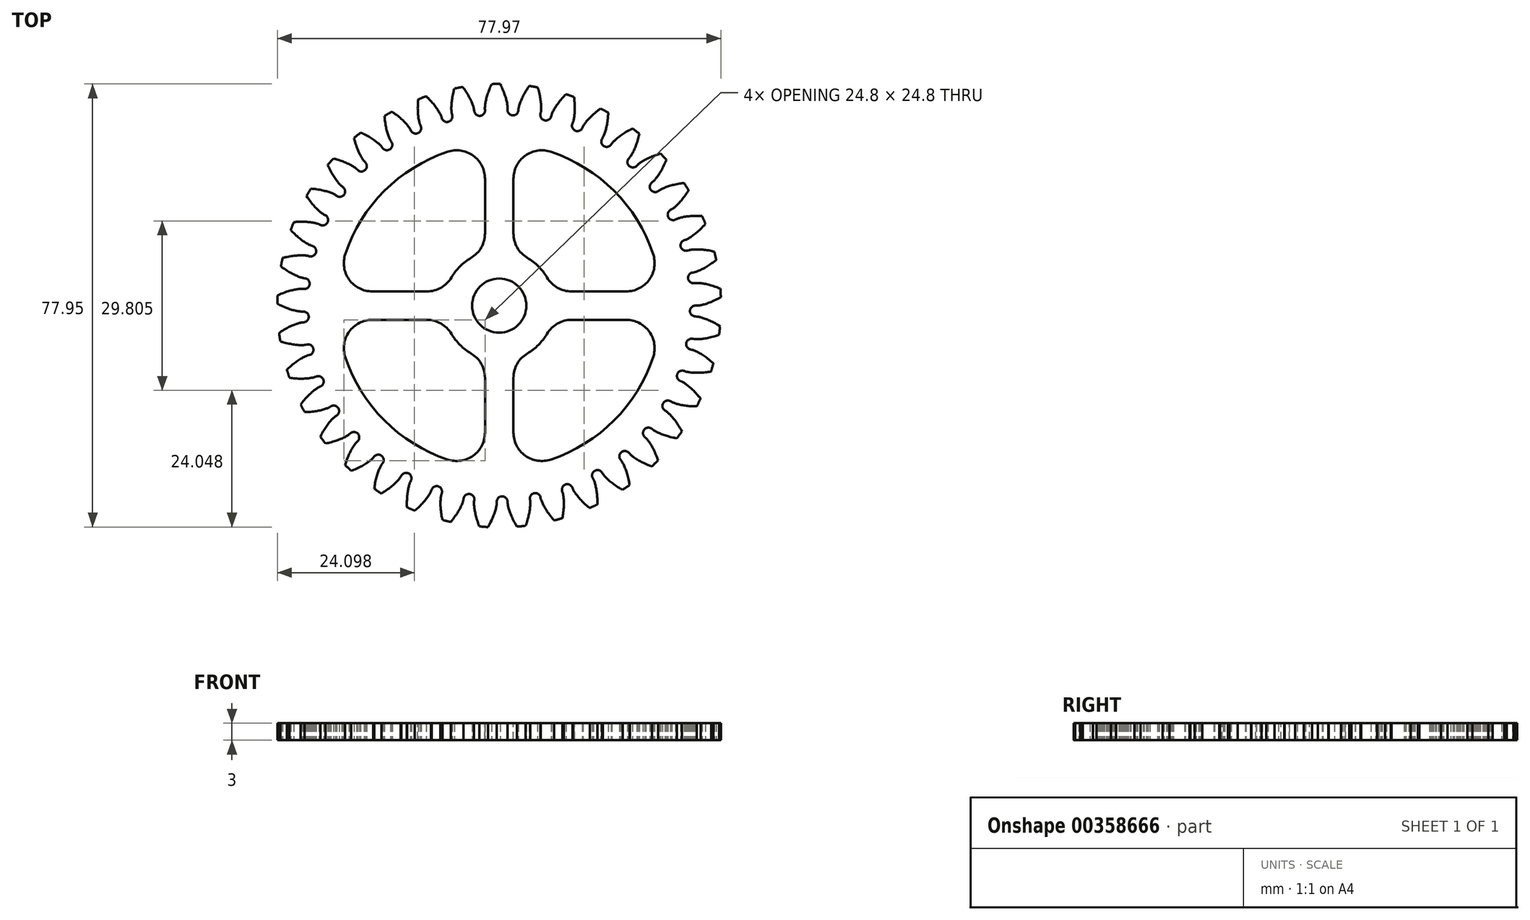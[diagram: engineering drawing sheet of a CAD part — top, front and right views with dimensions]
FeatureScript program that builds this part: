
annotation { "Feature Type Name" : "Feature", "Feature Type Description" : "" }
export const myFeature = defineFeature(function(context is Context, id is Id, definition is map)
    precondition{}
    {
        {
            assignVariable(context, id + "F0", {"name" : "T", "anyValue" : 37});
        }
        {
            assignVariable(context, id + "F1", {"name" : "SP", "anyValue" : 4});
        }
        {
            var Q0;
            Q0=qCreatedBy(makeId("Top.planeOp"),FACE);
            var sketch = newSketch(context, id + "F2", { "sketchPlane" : qUnion([Q0])});
            skCircle(sketch, "E0", {"center": v(0, 0) * mm, "radius": 39 * mm});
            skCircle(sketch, "E1", {"center": v(0, 0) * mm, "radius": 37 * mm, "construction": true});
            skCircle(sketch, "E2", {"center": v(0, 0) * mm, "radius": 34.77 * mm, "construction": true});
            skCircle(sketch, "E3", {"center": v(0, 0) * mm, "radius": 34.5 * mm});
            skLineSegment(sketch, "E4", {"start": v(0, 0) * mm, "end": v(34.77, 0) * mm});
            skFitSpline(sketch, "E5", {"points": [v(34.77, 0) * mm, v(34.82, 0) * mm, v(34.97, 0.01) * mm, v(35.21, 0.05) * mm, v(35.55, 0.11) * mm, v(35.98, 0.22) * mm, v(36.5, 0.38) * mm, v(37.1, 0.6) * mm, v(37.8, 0.88) * mm, v(38.55, 1.25) * mm, v(39.37, 1.71) * mm], "startDerivative": vector(4.43, 0.16) * mm, "endDerivative": vector(16.9, 9.4) * mm});
            skLineSegment(sketch, "E6", {"start": v(0, 0) * mm, "end": v(38.99, -1.07) * mm, "construction": true});
            skLineSegment(sketch, "E7", {"start": v(0, 0) * mm, "end": v(37, 0.55) * mm, "construction": true});
            skFitSpline(sketch, "E8.MirrorCS", {"points": [v(34.72, -1.91) * mm, v(34.77, -1.92) * mm, v(34.91, -1.94) * mm, v(35.16, -1.99) * mm, v(35.5, -2.07) * mm, v(35.92, -2.2) * mm, v(36.43, -2.39) * mm, v(37.02, -2.64) * mm, v(37.69, -2.96) * mm, v(38.42, -3.37) * mm, v(39.22, -3.88) * mm], "startDerivative": vector(4.42, -0.4) * mm, "endDerivative": vector(16.36, -10.31) * mm});
            skLineSegment(sketch, "E9", {"start": v(0, 0) * mm, "end": v(34.72, -1.91) * mm});
            skSolve(sketch);
        }
        {
            var Q0;
            Q0=qCreatedBy(makeId("Top.planeOp"),FACE);
            var sketch = newSketch(context, id + "F3", { "sketchPlane" : qUnion([Q0])});
            skCircle(sketch, "E10", {"center": v(0, 0) * mm, "radius": 39 * mm});
            skSolve(sketch);
        }
        {
            var Q0;
            {var subQ0=sQuery(id+"F2.wireOp",EDGE,"E5");var subQ7=sQuery(id+"F2.wireOp",EDGE,"E0");var subQ8=makeQuery(id+"F2.imprint","INTERSECT",VERTEX,{"derivedFrom":[subQ7,subQ0]});Q0=makeQuery(id+"F2.imprint","IMPRINT",FACE,{"disambiguationData":[TD([[makeQuery(id+"F2.imprint","IMPRINT",EDGE,{"disambiguationData":[TD([[subQ8,1.0]])],"derivedFrom":subQ7}),1.0]])]});}
            extrude(context, id + "F4", {"entities" : qUnion([Q0]), "depth" : 6 * mm});
        }
        {
            var Q0;
            Q0=makeQuery(id+"F4.opExtrude","CAP_FACE",FACE,{"disambiguationData":[OSD([sQuery(id+"F2.wireOp",EDGE,"E0"),sQuery(id+"F2.wireOp",EDGE,"E3"),sQuery(id+"F2.wireOp",EDGE,"E4"),sQuery(id+"F2.wireOp",EDGE,"E5"),sQuery(id+"F2.wireOp",EDGE,"E8.MirrorCS"),sQuery(id+"F2.wireOp",EDGE,"E9")])],"isStart":true});
            var sketch = newSketch(context, id + "F5", { "sketchPlane" : qUnion([Q0])});
            skCircle(sketch, "E11", {"center": v(34.49, 0.95) * mm, "radius": 0.95 * mm});
            skSolve(sketch);
        }
        {
            var Q0;
            {var subQ1=makeQuery(id+"F4.opExtrude","CAP_EDGE",EDGE,{"disambiguationData":[OSD([sQuery(id+"F2.wireOp",EDGE,"E3")])],"isStart":true});Q0=makeQuery(id+"F5.imprint","IMPRINT",FACE,{"disambiguationData":[TD([[makeQuery(id+"F5.imprint","IMPRINT",EDGE,{"derivedFrom":subQ1}),-1.0]])]});}
            extrude(context, id + "F6", {"entities" : qUnion([Q0]), "operationType" : NewBodyOperationType.ADD, "oppositeDirection" : true, "depth" : 6 * mm});
        }
        {
            var Q0;
            Q0=makeQuery(id+"F3.imprint","IMPRINT",FACE,{"disambiguationData":[TD([[makeQuery(id+"F3.imprint","IMPRINT",EDGE,{"derivedFrom":sQuery(id+"F3.wireOp",EDGE,"E10")}),1.0]])]});
            extrude(context, id + "F7", {"entities" : qUnion([Q0]), "depth" : 3 * mm, "offsetDistance" : 25 * mm});
        }
        {
            var Q0;
            Q0=makeQuery(id+"F4.opExtrude","SWEPT_BODY",BODY,{"disambiguationData":[OSD([sQuery(id+"F2.wireOp",EDGE,"E0"),sQuery(id+"F2.wireOp",EDGE,"E3"),sQuery(id+"F2.wireOp",EDGE,"E4"),sQuery(id+"F2.wireOp",EDGE,"E5"),sQuery(id+"F2.wireOp",EDGE,"E8.MirrorCS"),sQuery(id+"F2.wireOp",EDGE,"E9")])]});
            var Q1;
            Q1=makeQuery(id+"F7.opExtrude","CAP_EDGE",EDGE,{"disambiguationData":[OSD([sQuery(id+"F3.wireOp",EDGE,"E10")])],"isStart":false});
            circularPattern(context, id + "F8", {"entities" : qUnion([Q0]), "axis" : qUnion([Q1]), "angle" : 360 * degree, "instanceCount" : getVariable(context, 'T'), "equalSpace" : true});
        }
        {
            var Q0;
            Q0=makeQuery(id+"F8.opPattern","COPY",BODY,{"derivedFrom":makeQuery(id+"F4.opExtrude","SWEPT_BODY",BODY,{"disambiguationData":[OSD([sQuery(id+"F2.wireOp",EDGE,"E0"),sQuery(id+"F2.wireOp",EDGE,"E3"),sQuery(id+"F2.wireOp",EDGE,"E4"),sQuery(id+"F2.wireOp",EDGE,"E5"),sQuery(id+"F2.wireOp",EDGE,"E8.MirrorCS"),sQuery(id+"F2.wireOp",EDGE,"E9")])]}),"instanceName":"5"});
            var Q1;
            Q1=makeQuery(id+"F8.opPattern","COPY",BODY,{"derivedFrom":makeQuery(id+"F4.opExtrude","SWEPT_BODY",BODY,{"disambiguationData":[OSD([sQuery(id+"F2.wireOp",EDGE,"E0"),sQuery(id+"F2.wireOp",EDGE,"E3"),sQuery(id+"F2.wireOp",EDGE,"E4"),sQuery(id+"F2.wireOp",EDGE,"E5"),sQuery(id+"F2.wireOp",EDGE,"E8.MirrorCS"),sQuery(id+"F2.wireOp",EDGE,"E9")])]}),"instanceName":"6"});
            var Q2;
            Q2=makeQuery(id+"F8.opPattern","COPY",BODY,{"derivedFrom":makeQuery(id+"F4.opExtrude","SWEPT_BODY",BODY,{"disambiguationData":[OSD([sQuery(id+"F2.wireOp",EDGE,"E0"),sQuery(id+"F2.wireOp",EDGE,"E3"),sQuery(id+"F2.wireOp",EDGE,"E4"),sQuery(id+"F2.wireOp",EDGE,"E5"),sQuery(id+"F2.wireOp",EDGE,"E8.MirrorCS"),sQuery(id+"F2.wireOp",EDGE,"E9")])]}),"instanceName":"7"});
            var Q3;
            Q3=makeQuery(id+"F8.opPattern","COPY",BODY,{"derivedFrom":makeQuery(id+"F4.opExtrude","SWEPT_BODY",BODY,{"disambiguationData":[OSD([sQuery(id+"F2.wireOp",EDGE,"E0"),sQuery(id+"F2.wireOp",EDGE,"E3"),sQuery(id+"F2.wireOp",EDGE,"E4"),sQuery(id+"F2.wireOp",EDGE,"E5"),sQuery(id+"F2.wireOp",EDGE,"E8.MirrorCS"),sQuery(id+"F2.wireOp",EDGE,"E9")])]}),"instanceName":"8"});
            var Q4;
            Q4=makeQuery(id+"F8.opPattern","COPY",BODY,{"derivedFrom":makeQuery(id+"F4.opExtrude","SWEPT_BODY",BODY,{"disambiguationData":[OSD([sQuery(id+"F2.wireOp",EDGE,"E0"),sQuery(id+"F2.wireOp",EDGE,"E3"),sQuery(id+"F2.wireOp",EDGE,"E4"),sQuery(id+"F2.wireOp",EDGE,"E5"),sQuery(id+"F2.wireOp",EDGE,"E8.MirrorCS"),sQuery(id+"F2.wireOp",EDGE,"E9")])]}),"instanceName":"9"});
            var Q5;
            Q5=makeQuery(id+"F8.opPattern","COPY",BODY,{"derivedFrom":makeQuery(id+"F4.opExtrude","SWEPT_BODY",BODY,{"disambiguationData":[OSD([sQuery(id+"F2.wireOp",EDGE,"E0"),sQuery(id+"F2.wireOp",EDGE,"E3"),sQuery(id+"F2.wireOp",EDGE,"E4"),sQuery(id+"F2.wireOp",EDGE,"E5"),sQuery(id+"F2.wireOp",EDGE,"E8.MirrorCS"),sQuery(id+"F2.wireOp",EDGE,"E9")])]}),"instanceName":"10"});
            var Q6;
            Q6=makeQuery(id+"F8.opPattern","COPY",BODY,{"derivedFrom":makeQuery(id+"F4.opExtrude","SWEPT_BODY",BODY,{"disambiguationData":[OSD([sQuery(id+"F2.wireOp",EDGE,"E0"),sQuery(id+"F2.wireOp",EDGE,"E3"),sQuery(id+"F2.wireOp",EDGE,"E4"),sQuery(id+"F2.wireOp",EDGE,"E5"),sQuery(id+"F2.wireOp",EDGE,"E8.MirrorCS"),sQuery(id+"F2.wireOp",EDGE,"E9")])]}),"instanceName":"11"});
            var Q7;
            Q7=makeQuery(id+"F8.opPattern","COPY",BODY,{"derivedFrom":makeQuery(id+"F4.opExtrude","SWEPT_BODY",BODY,{"disambiguationData":[OSD([sQuery(id+"F2.wireOp",EDGE,"E0"),sQuery(id+"F2.wireOp",EDGE,"E3"),sQuery(id+"F2.wireOp",EDGE,"E4"),sQuery(id+"F2.wireOp",EDGE,"E5"),sQuery(id+"F2.wireOp",EDGE,"E8.MirrorCS"),sQuery(id+"F2.wireOp",EDGE,"E9")])]}),"instanceName":"12"});
            var Q8;
            Q8=makeQuery(id+"F8.opPattern","COPY",BODY,{"derivedFrom":makeQuery(id+"F4.opExtrude","SWEPT_BODY",BODY,{"disambiguationData":[OSD([sQuery(id+"F2.wireOp",EDGE,"E0"),sQuery(id+"F2.wireOp",EDGE,"E3"),sQuery(id+"F2.wireOp",EDGE,"E4"),sQuery(id+"F2.wireOp",EDGE,"E5"),sQuery(id+"F2.wireOp",EDGE,"E8.MirrorCS"),sQuery(id+"F2.wireOp",EDGE,"E9")])]}),"instanceName":"13"});
            var Q9;
            Q9=makeQuery(id+"F8.opPattern","COPY",BODY,{"derivedFrom":makeQuery(id+"F4.opExtrude","SWEPT_BODY",BODY,{"disambiguationData":[OSD([sQuery(id+"F2.wireOp",EDGE,"E0"),sQuery(id+"F2.wireOp",EDGE,"E3"),sQuery(id+"F2.wireOp",EDGE,"E4"),sQuery(id+"F2.wireOp",EDGE,"E5"),sQuery(id+"F2.wireOp",EDGE,"E8.MirrorCS"),sQuery(id+"F2.wireOp",EDGE,"E9")])]}),"instanceName":"14"});
            var Q10;
            Q10=makeQuery(id+"F8.opPattern","COPY",BODY,{"derivedFrom":makeQuery(id+"F4.opExtrude","SWEPT_BODY",BODY,{"disambiguationData":[OSD([sQuery(id+"F2.wireOp",EDGE,"E0"),sQuery(id+"F2.wireOp",EDGE,"E3"),sQuery(id+"F2.wireOp",EDGE,"E4"),sQuery(id+"F2.wireOp",EDGE,"E5"),sQuery(id+"F2.wireOp",EDGE,"E8.MirrorCS"),sQuery(id+"F2.wireOp",EDGE,"E9")])]}),"instanceName":"15"});
            var Q11;
            Q11=makeQuery(id+"F8.opPattern","COPY",BODY,{"derivedFrom":makeQuery(id+"F4.opExtrude","SWEPT_BODY",BODY,{"disambiguationData":[OSD([sQuery(id+"F2.wireOp",EDGE,"E0"),sQuery(id+"F2.wireOp",EDGE,"E3"),sQuery(id+"F2.wireOp",EDGE,"E4"),sQuery(id+"F2.wireOp",EDGE,"E5"),sQuery(id+"F2.wireOp",EDGE,"E8.MirrorCS"),sQuery(id+"F2.wireOp",EDGE,"E9")])]}),"instanceName":"16"});
            var Q12;
            Q12=makeQuery(id+"F8.opPattern","COPY",BODY,{"derivedFrom":makeQuery(id+"F4.opExtrude","SWEPT_BODY",BODY,{"disambiguationData":[OSD([sQuery(id+"F2.wireOp",EDGE,"E0"),sQuery(id+"F2.wireOp",EDGE,"E3"),sQuery(id+"F2.wireOp",EDGE,"E4"),sQuery(id+"F2.wireOp",EDGE,"E5"),sQuery(id+"F2.wireOp",EDGE,"E8.MirrorCS"),sQuery(id+"F2.wireOp",EDGE,"E9")])]}),"instanceName":"17"});
            var Q13;
            Q13=makeQuery(id+"F8.opPattern","COPY",BODY,{"derivedFrom":makeQuery(id+"F4.opExtrude","SWEPT_BODY",BODY,{"disambiguationData":[OSD([sQuery(id+"F2.wireOp",EDGE,"E0"),sQuery(id+"F2.wireOp",EDGE,"E3"),sQuery(id+"F2.wireOp",EDGE,"E4"),sQuery(id+"F2.wireOp",EDGE,"E5"),sQuery(id+"F2.wireOp",EDGE,"E8.MirrorCS"),sQuery(id+"F2.wireOp",EDGE,"E9")])]}),"instanceName":"18"});
            var Q14;
            Q14=makeQuery(id+"F8.opPattern","COPY",BODY,{"derivedFrom":makeQuery(id+"F4.opExtrude","SWEPT_BODY",BODY,{"disambiguationData":[OSD([sQuery(id+"F2.wireOp",EDGE,"E0"),sQuery(id+"F2.wireOp",EDGE,"E3"),sQuery(id+"F2.wireOp",EDGE,"E4"),sQuery(id+"F2.wireOp",EDGE,"E5"),sQuery(id+"F2.wireOp",EDGE,"E8.MirrorCS"),sQuery(id+"F2.wireOp",EDGE,"E9")])]}),"instanceName":"19"});
            var Q15;
            Q15=makeQuery(id+"F8.opPattern","COPY",BODY,{"derivedFrom":makeQuery(id+"F4.opExtrude","SWEPT_BODY",BODY,{"disambiguationData":[OSD([sQuery(id+"F2.wireOp",EDGE,"E0"),sQuery(id+"F2.wireOp",EDGE,"E3"),sQuery(id+"F2.wireOp",EDGE,"E4"),sQuery(id+"F2.wireOp",EDGE,"E5"),sQuery(id+"F2.wireOp",EDGE,"E8.MirrorCS"),sQuery(id+"F2.wireOp",EDGE,"E9")])]}),"instanceName":"20"});
            var Q16;
            Q16=makeQuery(id+"F8.opPattern","COPY",BODY,{"derivedFrom":makeQuery(id+"F4.opExtrude","SWEPT_BODY",BODY,{"disambiguationData":[OSD([sQuery(id+"F2.wireOp",EDGE,"E0"),sQuery(id+"F2.wireOp",EDGE,"E3"),sQuery(id+"F2.wireOp",EDGE,"E4"),sQuery(id+"F2.wireOp",EDGE,"E5"),sQuery(id+"F2.wireOp",EDGE,"E8.MirrorCS"),sQuery(id+"F2.wireOp",EDGE,"E9")])]}),"instanceName":"21"});
            var Q17;
            Q17=makeQuery(id+"F8.opPattern","COPY",BODY,{"derivedFrom":makeQuery(id+"F4.opExtrude","SWEPT_BODY",BODY,{"disambiguationData":[OSD([sQuery(id+"F2.wireOp",EDGE,"E0"),sQuery(id+"F2.wireOp",EDGE,"E3"),sQuery(id+"F2.wireOp",EDGE,"E4"),sQuery(id+"F2.wireOp",EDGE,"E5"),sQuery(id+"F2.wireOp",EDGE,"E8.MirrorCS"),sQuery(id+"F2.wireOp",EDGE,"E9")])]}),"instanceName":"22"});
            var Q18;
            Q18=makeQuery(id+"F8.opPattern","COPY",BODY,{"derivedFrom":makeQuery(id+"F4.opExtrude","SWEPT_BODY",BODY,{"disambiguationData":[OSD([sQuery(id+"F2.wireOp",EDGE,"E0"),sQuery(id+"F2.wireOp",EDGE,"E3"),sQuery(id+"F2.wireOp",EDGE,"E4"),sQuery(id+"F2.wireOp",EDGE,"E5"),sQuery(id+"F2.wireOp",EDGE,"E8.MirrorCS"),sQuery(id+"F2.wireOp",EDGE,"E9")])]}),"instanceName":"23"});
            var Q19;
            Q19=makeQuery(id+"F8.opPattern","COPY",BODY,{"derivedFrom":makeQuery(id+"F4.opExtrude","SWEPT_BODY",BODY,{"disambiguationData":[OSD([sQuery(id+"F2.wireOp",EDGE,"E0"),sQuery(id+"F2.wireOp",EDGE,"E3"),sQuery(id+"F2.wireOp",EDGE,"E4"),sQuery(id+"F2.wireOp",EDGE,"E5"),sQuery(id+"F2.wireOp",EDGE,"E8.MirrorCS"),sQuery(id+"F2.wireOp",EDGE,"E9")])]}),"instanceName":"24"});
            var Q20;
            Q20=makeQuery(id+"F8.opPattern","COPY",BODY,{"derivedFrom":makeQuery(id+"F4.opExtrude","SWEPT_BODY",BODY,{"disambiguationData":[OSD([sQuery(id+"F2.wireOp",EDGE,"E0"),sQuery(id+"F2.wireOp",EDGE,"E3"),sQuery(id+"F2.wireOp",EDGE,"E4"),sQuery(id+"F2.wireOp",EDGE,"E5"),sQuery(id+"F2.wireOp",EDGE,"E8.MirrorCS"),sQuery(id+"F2.wireOp",EDGE,"E9")])]}),"instanceName":"25"});
            var Q21;
            Q21=makeQuery(id+"F8.opPattern","COPY",BODY,{"derivedFrom":makeQuery(id+"F4.opExtrude","SWEPT_BODY",BODY,{"disambiguationData":[OSD([sQuery(id+"F2.wireOp",EDGE,"E0"),sQuery(id+"F2.wireOp",EDGE,"E3"),sQuery(id+"F2.wireOp",EDGE,"E4"),sQuery(id+"F2.wireOp",EDGE,"E5"),sQuery(id+"F2.wireOp",EDGE,"E8.MirrorCS"),sQuery(id+"F2.wireOp",EDGE,"E9")])]}),"instanceName":"26"});
            var Q22;
            Q22=makeQuery(id+"F8.opPattern","COPY",BODY,{"derivedFrom":makeQuery(id+"F4.opExtrude","SWEPT_BODY",BODY,{"disambiguationData":[OSD([sQuery(id+"F2.wireOp",EDGE,"E0"),sQuery(id+"F2.wireOp",EDGE,"E3"),sQuery(id+"F2.wireOp",EDGE,"E4"),sQuery(id+"F2.wireOp",EDGE,"E5"),sQuery(id+"F2.wireOp",EDGE,"E8.MirrorCS"),sQuery(id+"F2.wireOp",EDGE,"E9")])]}),"instanceName":"27"});
            var Q23;
            Q23=makeQuery(id+"F8.opPattern","COPY",BODY,{"derivedFrom":makeQuery(id+"F4.opExtrude","SWEPT_BODY",BODY,{"disambiguationData":[OSD([sQuery(id+"F2.wireOp",EDGE,"E0"),sQuery(id+"F2.wireOp",EDGE,"E3"),sQuery(id+"F2.wireOp",EDGE,"E4"),sQuery(id+"F2.wireOp",EDGE,"E5"),sQuery(id+"F2.wireOp",EDGE,"E8.MirrorCS"),sQuery(id+"F2.wireOp",EDGE,"E9")])]}),"instanceName":"28"});
            var Q24;
            Q24=makeQuery(id+"F8.opPattern","COPY",BODY,{"derivedFrom":makeQuery(id+"F4.opExtrude","SWEPT_BODY",BODY,{"disambiguationData":[OSD([sQuery(id+"F2.wireOp",EDGE,"E0"),sQuery(id+"F2.wireOp",EDGE,"E3"),sQuery(id+"F2.wireOp",EDGE,"E4"),sQuery(id+"F2.wireOp",EDGE,"E5"),sQuery(id+"F2.wireOp",EDGE,"E8.MirrorCS"),sQuery(id+"F2.wireOp",EDGE,"E9")])]}),"instanceName":"29"});
            var Q25;
            Q25=makeQuery(id+"F4.opExtrude","SWEPT_BODY",BODY,{"disambiguationData":[OSD([sQuery(id+"F2.wireOp",EDGE,"E0"),sQuery(id+"F2.wireOp",EDGE,"E3"),sQuery(id+"F2.wireOp",EDGE,"E4"),sQuery(id+"F2.wireOp",EDGE,"E5"),sQuery(id+"F2.wireOp",EDGE,"E8.MirrorCS"),sQuery(id+"F2.wireOp",EDGE,"E9")])]});
            var Q26;
            Q26=makeQuery(id+"F8.opPattern","COPY",BODY,{"derivedFrom":makeQuery(id+"F4.opExtrude","SWEPT_BODY",BODY,{"disambiguationData":[OSD([sQuery(id+"F2.wireOp",EDGE,"E0"),sQuery(id+"F2.wireOp",EDGE,"E3"),sQuery(id+"F2.wireOp",EDGE,"E4"),sQuery(id+"F2.wireOp",EDGE,"E5"),sQuery(id+"F2.wireOp",EDGE,"E8.MirrorCS"),sQuery(id+"F2.wireOp",EDGE,"E9")])]}),"instanceName":"1"});
            var Q27;
            Q27=makeQuery(id+"F8.opPattern","COPY",BODY,{"derivedFrom":makeQuery(id+"F4.opExtrude","SWEPT_BODY",BODY,{"disambiguationData":[OSD([sQuery(id+"F2.wireOp",EDGE,"E0"),sQuery(id+"F2.wireOp",EDGE,"E3"),sQuery(id+"F2.wireOp",EDGE,"E4"),sQuery(id+"F2.wireOp",EDGE,"E5"),sQuery(id+"F2.wireOp",EDGE,"E8.MirrorCS"),sQuery(id+"F2.wireOp",EDGE,"E9")])]}),"instanceName":"2"});
            var Q28;
            Q28=makeQuery(id+"F8.opPattern","COPY",BODY,{"derivedFrom":makeQuery(id+"F4.opExtrude","SWEPT_BODY",BODY,{"disambiguationData":[OSD([sQuery(id+"F2.wireOp",EDGE,"E0"),sQuery(id+"F2.wireOp",EDGE,"E3"),sQuery(id+"F2.wireOp",EDGE,"E4"),sQuery(id+"F2.wireOp",EDGE,"E5"),sQuery(id+"F2.wireOp",EDGE,"E8.MirrorCS"),sQuery(id+"F2.wireOp",EDGE,"E9")])]}),"instanceName":"3"});
            var Q29;
            Q29=makeQuery(id+"F8.opPattern","COPY",BODY,{"derivedFrom":makeQuery(id+"F4.opExtrude","SWEPT_BODY",BODY,{"disambiguationData":[OSD([sQuery(id+"F2.wireOp",EDGE,"E0"),sQuery(id+"F2.wireOp",EDGE,"E3"),sQuery(id+"F2.wireOp",EDGE,"E4"),sQuery(id+"F2.wireOp",EDGE,"E5"),sQuery(id+"F2.wireOp",EDGE,"E8.MirrorCS"),sQuery(id+"F2.wireOp",EDGE,"E9")])]}),"instanceName":"4"});
            var Q30;
            Q30=makeQuery(id+"F8.opPattern","COPY",BODY,{"derivedFrom":makeQuery(id+"F4.opExtrude","SWEPT_BODY",BODY,{"disambiguationData":[OSD([sQuery(id+"F2.wireOp",EDGE,"E0"),sQuery(id+"F2.wireOp",EDGE,"E3"),sQuery(id+"F2.wireOp",EDGE,"E5"),sQuery(id+"F2.wireOp",EDGE,"E8.MirrorCS")])]}),"instanceName":"30"});
            var Q31;
            Q31=makeQuery(id+"F8.opPattern","COPY",BODY,{"derivedFrom":makeQuery(id+"F4.opExtrude","SWEPT_BODY",BODY,{"disambiguationData":[OSD([sQuery(id+"F2.wireOp",EDGE,"E0"),sQuery(id+"F2.wireOp",EDGE,"E3"),sQuery(id+"F2.wireOp",EDGE,"E5"),sQuery(id+"F2.wireOp",EDGE,"E8.MirrorCS")])]}),"instanceName":"31"});
            var Q32;
            Q32=makeQuery(id+"F8.opPattern","COPY",BODY,{"derivedFrom":makeQuery(id+"F4.opExtrude","SWEPT_BODY",BODY,{"disambiguationData":[OSD([sQuery(id+"F2.wireOp",EDGE,"E0"),sQuery(id+"F2.wireOp",EDGE,"E3"),sQuery(id+"F2.wireOp",EDGE,"E5"),sQuery(id+"F2.wireOp",EDGE,"E8.MirrorCS")])]}),"instanceName":"32"});
            var Q33;
            Q33=makeQuery(id+"F8.opPattern","COPY",BODY,{"derivedFrom":makeQuery(id+"F4.opExtrude","SWEPT_BODY",BODY,{"disambiguationData":[OSD([sQuery(id+"F2.wireOp",EDGE,"E0"),sQuery(id+"F2.wireOp",EDGE,"E3"),sQuery(id+"F2.wireOp",EDGE,"E5"),sQuery(id+"F2.wireOp",EDGE,"E8.MirrorCS")])]}),"instanceName":"33"});
            var Q34;
            Q34=makeQuery(id+"F8.opPattern","COPY",BODY,{"derivedFrom":makeQuery(id+"F4.opExtrude","SWEPT_BODY",BODY,{"disambiguationData":[OSD([sQuery(id+"F2.wireOp",EDGE,"E0"),sQuery(id+"F2.wireOp",EDGE,"E3"),sQuery(id+"F2.wireOp",EDGE,"E5"),sQuery(id+"F2.wireOp",EDGE,"E8.MirrorCS")])]}),"instanceName":"34"});
            var Q35;
            Q35=makeQuery(id+"F8.opPattern","COPY",BODY,{"derivedFrom":makeQuery(id+"F4.opExtrude","SWEPT_BODY",BODY,{"disambiguationData":[OSD([sQuery(id+"F2.wireOp",EDGE,"E0"),sQuery(id+"F2.wireOp",EDGE,"E3"),sQuery(id+"F2.wireOp",EDGE,"E5"),sQuery(id+"F2.wireOp",EDGE,"E8.MirrorCS")])]}),"instanceName":"35"});
            var Q36;
            Q36=makeQuery(id+"F8.opPattern","COPY",BODY,{"derivedFrom":makeQuery(id+"F4.opExtrude","SWEPT_BODY",BODY,{"disambiguationData":[OSD([sQuery(id+"F2.wireOp",EDGE,"E0"),sQuery(id+"F2.wireOp",EDGE,"E3"),sQuery(id+"F2.wireOp",EDGE,"E5"),sQuery(id+"F2.wireOp",EDGE,"E8.MirrorCS")])]}),"instanceName":"36"});
            var Q37;
            Q37=makeQuery(id+"F8.opPattern","COPY",BODY,{"derivedFrom":makeQuery(id+"F4.opExtrude","SWEPT_BODY",BODY,{"disambiguationData":[OSD([sQuery(id+"F2.wireOp",EDGE,"E0"),sQuery(id+"F2.wireOp",EDGE,"E3"),sQuery(id+"F2.wireOp",EDGE,"E5"),sQuery(id+"F2.wireOp",EDGE,"E8.MirrorCS")])]}),"instanceName":"37"});
            var Q38;
            Q38=makeQuery(id+"F8.opPattern","COPY",BODY,{"derivedFrom":makeQuery(id+"F4.opExtrude","SWEPT_BODY",BODY,{"disambiguationData":[OSD([sQuery(id+"F2.wireOp",EDGE,"E0"),sQuery(id+"F2.wireOp",EDGE,"E3"),sQuery(id+"F2.wireOp",EDGE,"E5"),sQuery(id+"F2.wireOp",EDGE,"E8.MirrorCS")])]}),"instanceName":"38"});
            var Q39;
            Q39=makeQuery(id+"F8.opPattern","COPY",BODY,{"derivedFrom":makeQuery(id+"F4.opExtrude","SWEPT_BODY",BODY,{"disambiguationData":[OSD([sQuery(id+"F2.wireOp",EDGE,"E0"),sQuery(id+"F2.wireOp",EDGE,"E3"),sQuery(id+"F2.wireOp",EDGE,"E5"),sQuery(id+"F2.wireOp",EDGE,"E8.MirrorCS")])]}),"instanceName":"39"});
            var Q40;
            Q40=makeQuery(id+"F8.opPattern","COPY",BODY,{"derivedFrom":makeQuery(id+"F4.opExtrude","SWEPT_BODY",BODY,{"disambiguationData":[OSD([sQuery(id+"F2.wireOp",EDGE,"E0"),sQuery(id+"F2.wireOp",EDGE,"E3"),sQuery(id+"F2.wireOp",EDGE,"E5"),sQuery(id+"F2.wireOp",EDGE,"E8.MirrorCS")])]}),"instanceName":"40"});
            var Q41;
            Q41=makeQuery(id+"F8.opPattern","COPY",BODY,{"derivedFrom":makeQuery(id+"F4.opExtrude","SWEPT_BODY",BODY,{"disambiguationData":[OSD([sQuery(id+"F2.wireOp",EDGE,"E0"),sQuery(id+"F2.wireOp",EDGE,"E3"),sQuery(id+"F2.wireOp",EDGE,"E5"),sQuery(id+"F2.wireOp",EDGE,"E8.MirrorCS")])]}),"instanceName":"41"});
            var Q42;
            Q42=makeQuery(id+"F8.opPattern","COPY",BODY,{"derivedFrom":makeQuery(id+"F4.opExtrude","SWEPT_BODY",BODY,{"disambiguationData":[OSD([sQuery(id+"F2.wireOp",EDGE,"E0"),sQuery(id+"F2.wireOp",EDGE,"E3"),sQuery(id+"F2.wireOp",EDGE,"E5"),sQuery(id+"F2.wireOp",EDGE,"E8.MirrorCS")])]}),"instanceName":"42"});
            var Q43;
            Q43=makeQuery(id+"F8.opPattern","COPY",BODY,{"derivedFrom":makeQuery(id+"F4.opExtrude","SWEPT_BODY",BODY,{"disambiguationData":[OSD([sQuery(id+"F2.wireOp",EDGE,"E0"),sQuery(id+"F2.wireOp",EDGE,"E3"),sQuery(id+"F2.wireOp",EDGE,"E5"),sQuery(id+"F2.wireOp",EDGE,"E8.MirrorCS")])]}),"instanceName":"43"});
            var Q44;
            Q44=makeQuery(id+"F8.opPattern","COPY",BODY,{"derivedFrom":makeQuery(id+"F4.opExtrude","SWEPT_BODY",BODY,{"disambiguationData":[OSD([sQuery(id+"F2.wireOp",EDGE,"E0"),sQuery(id+"F2.wireOp",EDGE,"E3"),sQuery(id+"F2.wireOp",EDGE,"E5"),sQuery(id+"F2.wireOp",EDGE,"E8.MirrorCS")])]}),"instanceName":"44"});
            var Q45;
            Q45=makeQuery(id+"F8.opPattern","COPY",BODY,{"derivedFrom":makeQuery(id+"F4.opExtrude","SWEPT_BODY",BODY,{"disambiguationData":[OSD([sQuery(id+"F2.wireOp",EDGE,"E0"),sQuery(id+"F2.wireOp",EDGE,"E3"),sQuery(id+"F2.wireOp",EDGE,"E5"),sQuery(id+"F2.wireOp",EDGE,"E8.MirrorCS")])]}),"instanceName":"45"});
            var Q46;
            Q46=makeQuery(id+"F8.opPattern","COPY",BODY,{"derivedFrom":makeQuery(id+"F4.opExtrude","SWEPT_BODY",BODY,{"disambiguationData":[OSD([sQuery(id+"F2.wireOp",EDGE,"E0"),sQuery(id+"F2.wireOp",EDGE,"E3"),sQuery(id+"F2.wireOp",EDGE,"E5"),sQuery(id+"F2.wireOp",EDGE,"E8.MirrorCS")])]}),"instanceName":"46"});
            var Q47;
            Q47=makeQuery(id+"F8.opPattern","COPY",BODY,{"derivedFrom":makeQuery(id+"F4.opExtrude","SWEPT_BODY",BODY,{"disambiguationData":[OSD([sQuery(id+"F2.wireOp",EDGE,"E0"),sQuery(id+"F2.wireOp",EDGE,"E3"),sQuery(id+"F2.wireOp",EDGE,"E5"),sQuery(id+"F2.wireOp",EDGE,"E8.MirrorCS")])]}),"instanceName":"47"});
            var Q48;
            Q48=makeQuery(id+"F8.opPattern","COPY",BODY,{"derivedFrom":makeQuery(id+"F4.opExtrude","SWEPT_BODY",BODY,{"disambiguationData":[OSD([sQuery(id+"F2.wireOp",EDGE,"E0"),sQuery(id+"F2.wireOp",EDGE,"E3"),sQuery(id+"F2.wireOp",EDGE,"E5"),sQuery(id+"F2.wireOp",EDGE,"E8.MirrorCS")])]}),"instanceName":"48"});
            var Q49;
            Q49=makeQuery(id+"F8.opPattern","COPY",BODY,{"derivedFrom":makeQuery(id+"F4.opExtrude","SWEPT_BODY",BODY,{"disambiguationData":[OSD([sQuery(id+"F2.wireOp",EDGE,"E0"),sQuery(id+"F2.wireOp",EDGE,"E3"),sQuery(id+"F2.wireOp",EDGE,"E5"),sQuery(id+"F2.wireOp",EDGE,"E8.MirrorCS")])]}),"instanceName":"49"});
            var Q50;
            Q50=makeQuery(id+"F8.opPattern","COPY",BODY,{"derivedFrom":makeQuery(id+"F4.opExtrude","SWEPT_BODY",BODY,{"disambiguationData":[OSD([sQuery(id+"F2.wireOp",EDGE,"E0"),sQuery(id+"F2.wireOp",EDGE,"E3"),sQuery(id+"F2.wireOp",EDGE,"E5"),sQuery(id+"F2.wireOp",EDGE,"E8.MirrorCS")])]}),"instanceName":"50"});
            var Q51;
            Q51=makeQuery(id+"F8.opPattern","COPY",BODY,{"derivedFrom":makeQuery(id+"F4.opExtrude","SWEPT_BODY",BODY,{"disambiguationData":[OSD([sQuery(id+"F2.wireOp",EDGE,"E0"),sQuery(id+"F2.wireOp",EDGE,"E3"),sQuery(id+"F2.wireOp",EDGE,"E5"),sQuery(id+"F2.wireOp",EDGE,"E8.MirrorCS")])]}),"instanceName":"51"});
            var Q52;
            Q52=makeQuery(id+"F8.opPattern","COPY",BODY,{"derivedFrom":makeQuery(id+"F4.opExtrude","SWEPT_BODY",BODY,{"disambiguationData":[OSD([sQuery(id+"F2.wireOp",EDGE,"E0"),sQuery(id+"F2.wireOp",EDGE,"E3"),sQuery(id+"F2.wireOp",EDGE,"E5"),sQuery(id+"F2.wireOp",EDGE,"E8.MirrorCS")])]}),"instanceName":"52"});
            var Q53;
            Q53=makeQuery(id+"F8.opPattern","COPY",BODY,{"derivedFrom":makeQuery(id+"F4.opExtrude","SWEPT_BODY",BODY,{"disambiguationData":[OSD([sQuery(id+"F2.wireOp",EDGE,"E0"),sQuery(id+"F2.wireOp",EDGE,"E3"),sQuery(id+"F2.wireOp",EDGE,"E5"),sQuery(id+"F2.wireOp",EDGE,"E8.MirrorCS")])]}),"instanceName":"53"});
            var Q54;
            Q54=makeQuery(id+"F8.opPattern","COPY",BODY,{"derivedFrom":makeQuery(id+"F4.opExtrude","SWEPT_BODY",BODY,{"disambiguationData":[OSD([sQuery(id+"F2.wireOp",EDGE,"E0"),sQuery(id+"F2.wireOp",EDGE,"E3"),sQuery(id+"F2.wireOp",EDGE,"E5"),sQuery(id+"F2.wireOp",EDGE,"E8.MirrorCS")])]}),"instanceName":"54"});
            var Q55;
            Q55=makeQuery(id+"F8.opPattern","COPY",BODY,{"derivedFrom":makeQuery(id+"F4.opExtrude","SWEPT_BODY",BODY,{"disambiguationData":[OSD([sQuery(id+"F2.wireOp",EDGE,"E0"),sQuery(id+"F2.wireOp",EDGE,"E3"),sQuery(id+"F2.wireOp",EDGE,"E5"),sQuery(id+"F2.wireOp",EDGE,"E8.MirrorCS")])]}),"instanceName":"55"});
            var Q56;
            Q56=makeQuery(id+"F8.opPattern","COPY",BODY,{"derivedFrom":makeQuery(id+"F4.opExtrude","SWEPT_BODY",BODY,{"disambiguationData":[OSD([sQuery(id+"F2.wireOp",EDGE,"E0"),sQuery(id+"F2.wireOp",EDGE,"E3"),sQuery(id+"F2.wireOp",EDGE,"E5"),sQuery(id+"F2.wireOp",EDGE,"E8.MirrorCS")])]}),"instanceName":"56"});
            var Q57;
            Q57=makeQuery(id+"F8.opPattern","COPY",BODY,{"derivedFrom":makeQuery(id+"F4.opExtrude","SWEPT_BODY",BODY,{"disambiguationData":[OSD([sQuery(id+"F2.wireOp",EDGE,"E0"),sQuery(id+"F2.wireOp",EDGE,"E3"),sQuery(id+"F2.wireOp",EDGE,"E5"),sQuery(id+"F2.wireOp",EDGE,"E8.MirrorCS")])]}),"instanceName":"57"});
            var Q58;
            Q58=makeQuery(id+"F8.opPattern","COPY",BODY,{"derivedFrom":makeQuery(id+"F4.opExtrude","SWEPT_BODY",BODY,{"disambiguationData":[OSD([sQuery(id+"F2.wireOp",EDGE,"E0"),sQuery(id+"F2.wireOp",EDGE,"E3"),sQuery(id+"F2.wireOp",EDGE,"E5"),sQuery(id+"F2.wireOp",EDGE,"E8.MirrorCS")])]}),"instanceName":"58"});
            var Q59;
            Q59=makeQuery(id+"F8.opPattern","COPY",BODY,{"derivedFrom":makeQuery(id+"F4.opExtrude","SWEPT_BODY",BODY,{"disambiguationData":[OSD([sQuery(id+"F2.wireOp",EDGE,"E0"),sQuery(id+"F2.wireOp",EDGE,"E3"),sQuery(id+"F2.wireOp",EDGE,"E5"),sQuery(id+"F2.wireOp",EDGE,"E8.MirrorCS")])]}),"instanceName":"59"});
            var Q60;
            Q60=makeQuery(id+"F8.opPattern","COPY",BODY,{"derivedFrom":makeQuery(id+"F4.opExtrude","SWEPT_BODY",BODY,{"disambiguationData":[OSD([sQuery(id+"F2.wireOp",EDGE,"E0"),sQuery(id+"F2.wireOp",EDGE,"E3"),sQuery(id+"F2.wireOp",EDGE,"E5"),sQuery(id+"F2.wireOp",EDGE,"E8.MirrorCS")])]}),"instanceName":"60"});
            var Q61;
            Q61=makeQuery(id+"F8.opPattern","COPY",BODY,{"derivedFrom":makeQuery(id+"F4.opExtrude","SWEPT_BODY",BODY,{"disambiguationData":[OSD([sQuery(id+"F2.wireOp",EDGE,"E0"),sQuery(id+"F2.wireOp",EDGE,"E3"),sQuery(id+"F2.wireOp",EDGE,"E5"),sQuery(id+"F2.wireOp",EDGE,"E8.MirrorCS")])]}),"instanceName":"61"});
            var Q62;
            Q62=makeQuery(id+"F8.opPattern","COPY",BODY,{"derivedFrom":makeQuery(id+"F4.opExtrude","SWEPT_BODY",BODY,{"disambiguationData":[OSD([sQuery(id+"F2.wireOp",EDGE,"E0"),sQuery(id+"F2.wireOp",EDGE,"E3"),sQuery(id+"F2.wireOp",EDGE,"E5"),sQuery(id+"F2.wireOp",EDGE,"E8.MirrorCS")])]}),"instanceName":"62"});
            var Q63;
            Q63=makeQuery(id+"F8.opPattern","COPY",BODY,{"derivedFrom":makeQuery(id+"F4.opExtrude","SWEPT_BODY",BODY,{"disambiguationData":[OSD([sQuery(id+"F2.wireOp",EDGE,"E0"),sQuery(id+"F2.wireOp",EDGE,"E3"),sQuery(id+"F2.wireOp",EDGE,"E5"),sQuery(id+"F2.wireOp",EDGE,"E8.MirrorCS")])]}),"instanceName":"63"});
            var Q64;
            Q64=makeQuery(id+"F8.opPattern","COPY",BODY,{"derivedFrom":makeQuery(id+"F4.opExtrude","SWEPT_BODY",BODY,{"disambiguationData":[OSD([sQuery(id+"F2.wireOp",EDGE,"E0"),sQuery(id+"F2.wireOp",EDGE,"E3"),sQuery(id+"F2.wireOp",EDGE,"E5"),sQuery(id+"F2.wireOp",EDGE,"E8.MirrorCS")])]}),"instanceName":"64"});
            var Q65;
            Q65=makeQuery(id+"F8.opPattern","COPY",BODY,{"derivedFrom":makeQuery(id+"F4.opExtrude","SWEPT_BODY",BODY,{"disambiguationData":[OSD([sQuery(id+"F2.wireOp",EDGE,"E0"),sQuery(id+"F2.wireOp",EDGE,"E3"),sQuery(id+"F2.wireOp",EDGE,"E5"),sQuery(id+"F2.wireOp",EDGE,"E8.MirrorCS")])]}),"instanceName":"65"});
            var Q66;
            Q66=makeQuery(id+"F8.opPattern","COPY",BODY,{"derivedFrom":makeQuery(id+"F4.opExtrude","SWEPT_BODY",BODY,{"disambiguationData":[OSD([sQuery(id+"F2.wireOp",EDGE,"E0"),sQuery(id+"F2.wireOp",EDGE,"E3"),sQuery(id+"F2.wireOp",EDGE,"E5"),sQuery(id+"F2.wireOp",EDGE,"E8.MirrorCS")])]}),"instanceName":"66"});
            var Q67;
            Q67=makeQuery(id+"F8.opPattern","COPY",BODY,{"derivedFrom":makeQuery(id+"F4.opExtrude","SWEPT_BODY",BODY,{"disambiguationData":[OSD([sQuery(id+"F2.wireOp",EDGE,"E0"),sQuery(id+"F2.wireOp",EDGE,"E3"),sQuery(id+"F2.wireOp",EDGE,"E5"),sQuery(id+"F2.wireOp",EDGE,"E8.MirrorCS")])]}),"instanceName":"67"});
            var Q68;
            Q68=makeQuery(id+"F8.opPattern","COPY",BODY,{"derivedFrom":makeQuery(id+"F4.opExtrude","SWEPT_BODY",BODY,{"disambiguationData":[OSD([sQuery(id+"F2.wireOp",EDGE,"E0"),sQuery(id+"F2.wireOp",EDGE,"E3"),sQuery(id+"F2.wireOp",EDGE,"E5"),sQuery(id+"F2.wireOp",EDGE,"E8.MirrorCS")])]}),"instanceName":"68"});
            var Q69;
            Q69=makeQuery(id+"F8.opPattern","COPY",BODY,{"derivedFrom":makeQuery(id+"F4.opExtrude","SWEPT_BODY",BODY,{"disambiguationData":[OSD([sQuery(id+"F2.wireOp",EDGE,"E0"),sQuery(id+"F2.wireOp",EDGE,"E3"),sQuery(id+"F2.wireOp",EDGE,"E5"),sQuery(id+"F2.wireOp",EDGE,"E8.MirrorCS")])]}),"instanceName":"69"});
            var Q70;
            Q70=makeQuery(id+"F8.opPattern","COPY",BODY,{"derivedFrom":makeQuery(id+"F4.opExtrude","SWEPT_BODY",BODY,{"disambiguationData":[OSD([sQuery(id+"F2.wireOp",EDGE,"E0"),sQuery(id+"F2.wireOp",EDGE,"E3"),sQuery(id+"F2.wireOp",EDGE,"E5"),sQuery(id+"F2.wireOp",EDGE,"E8.MirrorCS")])]}),"instanceName":"70"});
            var Q71;
            Q71=makeQuery(id+"F8.opPattern","COPY",BODY,{"derivedFrom":makeQuery(id+"F4.opExtrude","SWEPT_BODY",BODY,{"disambiguationData":[OSD([sQuery(id+"F2.wireOp",EDGE,"E0"),sQuery(id+"F2.wireOp",EDGE,"E3"),sQuery(id+"F2.wireOp",EDGE,"E5"),sQuery(id+"F2.wireOp",EDGE,"E8.MirrorCS")])]}),"instanceName":"71"});
            var Q72;
            Q72=makeQuery(id+"F8.opPattern","COPY",BODY,{"derivedFrom":makeQuery(id+"F4.opExtrude","SWEPT_BODY",BODY,{"disambiguationData":[OSD([sQuery(id+"F2.wireOp",EDGE,"E0"),sQuery(id+"F2.wireOp",EDGE,"E3"),sQuery(id+"F2.wireOp",EDGE,"E5"),sQuery(id+"F2.wireOp",EDGE,"E8.MirrorCS")])]}),"instanceName":"72"});
            var Q73;
            Q73=makeQuery(id+"F8.opPattern","COPY",BODY,{"derivedFrom":makeQuery(id+"F4.opExtrude","SWEPT_BODY",BODY,{"disambiguationData":[OSD([sQuery(id+"F2.wireOp",EDGE,"E0"),sQuery(id+"F2.wireOp",EDGE,"E3"),sQuery(id+"F2.wireOp",EDGE,"E5"),sQuery(id+"F2.wireOp",EDGE,"E8.MirrorCS")])]}),"instanceName":"73"});
            var Q74;
            Q74=makeQuery(id+"F8.opPattern","COPY",BODY,{"derivedFrom":makeQuery(id+"F4.opExtrude","SWEPT_BODY",BODY,{"disambiguationData":[OSD([sQuery(id+"F2.wireOp",EDGE,"E0"),sQuery(id+"F2.wireOp",EDGE,"E3"),sQuery(id+"F2.wireOp",EDGE,"E5"),sQuery(id+"F2.wireOp",EDGE,"E8.MirrorCS")])]}),"instanceName":"74"});
            var Q75;
            Q75=makeQuery(id+"F8.opPattern","COPY",BODY,{"derivedFrom":makeQuery(id+"F4.opExtrude","SWEPT_BODY",BODY,{"disambiguationData":[OSD([sQuery(id+"F2.wireOp",EDGE,"E0"),sQuery(id+"F2.wireOp",EDGE,"E3"),sQuery(id+"F2.wireOp",EDGE,"E5"),sQuery(id+"F2.wireOp",EDGE,"E8.MirrorCS")])]}),"instanceName":"75"});
            var Q76;
            Q76=makeQuery(id+"F8.opPattern","COPY",BODY,{"derivedFrom":makeQuery(id+"F4.opExtrude","SWEPT_BODY",BODY,{"disambiguationData":[OSD([sQuery(id+"F2.wireOp",EDGE,"E0"),sQuery(id+"F2.wireOp",EDGE,"E3"),sQuery(id+"F2.wireOp",EDGE,"E5"),sQuery(id+"F2.wireOp",EDGE,"E8.MirrorCS")])]}),"instanceName":"76"});
            var Q77;
            Q77=makeQuery(id+"F8.opPattern","COPY",BODY,{"derivedFrom":makeQuery(id+"F4.opExtrude","SWEPT_BODY",BODY,{"disambiguationData":[OSD([sQuery(id+"F2.wireOp",EDGE,"E0"),sQuery(id+"F2.wireOp",EDGE,"E3"),sQuery(id+"F2.wireOp",EDGE,"E5"),sQuery(id+"F2.wireOp",EDGE,"E8.MirrorCS")])]}),"instanceName":"77"});
            var Q78;
            Q78=makeQuery(id+"F8.opPattern","COPY",BODY,{"derivedFrom":makeQuery(id+"F4.opExtrude","SWEPT_BODY",BODY,{"disambiguationData":[OSD([sQuery(id+"F2.wireOp",EDGE,"E0"),sQuery(id+"F2.wireOp",EDGE,"E3"),sQuery(id+"F2.wireOp",EDGE,"E5"),sQuery(id+"F2.wireOp",EDGE,"E8.MirrorCS")])]}),"instanceName":"78"});
            var Q79;
            Q79=makeQuery(id+"F8.opPattern","COPY",BODY,{"derivedFrom":makeQuery(id+"F4.opExtrude","SWEPT_BODY",BODY,{"disambiguationData":[OSD([sQuery(id+"F2.wireOp",EDGE,"E0"),sQuery(id+"F2.wireOp",EDGE,"E3"),sQuery(id+"F2.wireOp",EDGE,"E5"),sQuery(id+"F2.wireOp",EDGE,"E8.MirrorCS")])]}),"instanceName":"79"});
            var Q80;
            Q80=makeQuery(id+"F8.opPattern","COPY",BODY,{"derivedFrom":makeQuery(id+"F4.opExtrude","SWEPT_BODY",BODY,{"disambiguationData":[OSD([sQuery(id+"F2.wireOp",EDGE,"E0"),sQuery(id+"F2.wireOp",EDGE,"E3"),sQuery(id+"F2.wireOp",EDGE,"E5"),sQuery(id+"F2.wireOp",EDGE,"E8.MirrorCS")])]}),"instanceName":"80"});
            var Q81;
            Q81=makeQuery(id+"F8.opPattern","COPY",BODY,{"derivedFrom":makeQuery(id+"F4.opExtrude","SWEPT_BODY",BODY,{"disambiguationData":[OSD([sQuery(id+"F2.wireOp",EDGE,"E0"),sQuery(id+"F2.wireOp",EDGE,"E3"),sQuery(id+"F2.wireOp",EDGE,"E5"),sQuery(id+"F2.wireOp",EDGE,"E8.MirrorCS")])]}),"instanceName":"81"});
            var Q82;
            Q82=makeQuery(id+"F8.opPattern","COPY",BODY,{"derivedFrom":makeQuery(id+"F4.opExtrude","SWEPT_BODY",BODY,{"disambiguationData":[OSD([sQuery(id+"F2.wireOp",EDGE,"E0"),sQuery(id+"F2.wireOp",EDGE,"E3"),sQuery(id+"F2.wireOp",EDGE,"E5"),sQuery(id+"F2.wireOp",EDGE,"E8.MirrorCS")])]}),"instanceName":"82"});
            var Q83;
            Q83=makeQuery(id+"F8.opPattern","COPY",BODY,{"derivedFrom":makeQuery(id+"F4.opExtrude","SWEPT_BODY",BODY,{"disambiguationData":[OSD([sQuery(id+"F2.wireOp",EDGE,"E0"),sQuery(id+"F2.wireOp",EDGE,"E3"),sQuery(id+"F2.wireOp",EDGE,"E5"),sQuery(id+"F2.wireOp",EDGE,"E8.MirrorCS")])]}),"instanceName":"83"});
            var Q84;
            Q84=makeQuery(id+"F8.opPattern","COPY",BODY,{"derivedFrom":makeQuery(id+"F4.opExtrude","SWEPT_BODY",BODY,{"disambiguationData":[OSD([sQuery(id+"F2.wireOp",EDGE,"E0"),sQuery(id+"F2.wireOp",EDGE,"E3"),sQuery(id+"F2.wireOp",EDGE,"E5"),sQuery(id+"F2.wireOp",EDGE,"E8.MirrorCS")])]}),"instanceName":"84"});
            var Q85;
            Q85=makeQuery(id+"F8.opPattern","COPY",BODY,{"derivedFrom":makeQuery(id+"F4.opExtrude","SWEPT_BODY",BODY,{"disambiguationData":[OSD([sQuery(id+"F2.wireOp",EDGE,"E0"),sQuery(id+"F2.wireOp",EDGE,"E3"),sQuery(id+"F2.wireOp",EDGE,"E5"),sQuery(id+"F2.wireOp",EDGE,"E8.MirrorCS")])]}),"instanceName":"85"});
            var Q86;
            Q86=makeQuery(id+"F8.opPattern","COPY",BODY,{"derivedFrom":makeQuery(id+"F4.opExtrude","SWEPT_BODY",BODY,{"disambiguationData":[OSD([sQuery(id+"F2.wireOp",EDGE,"E0"),sQuery(id+"F2.wireOp",EDGE,"E3"),sQuery(id+"F2.wireOp",EDGE,"E5"),sQuery(id+"F2.wireOp",EDGE,"E8.MirrorCS")])]}),"instanceName":"86"});
            var Q87;
            Q87=makeQuery(id+"F8.opPattern","COPY",BODY,{"derivedFrom":makeQuery(id+"F4.opExtrude","SWEPT_BODY",BODY,{"disambiguationData":[OSD([sQuery(id+"F2.wireOp",EDGE,"E0"),sQuery(id+"F2.wireOp",EDGE,"E3"),sQuery(id+"F2.wireOp",EDGE,"E5"),sQuery(id+"F2.wireOp",EDGE,"E8.MirrorCS")])]}),"instanceName":"87"});
            var Q88;
            Q88=makeQuery(id+"F8.opPattern","COPY",BODY,{"derivedFrom":makeQuery(id+"F4.opExtrude","SWEPT_BODY",BODY,{"disambiguationData":[OSD([sQuery(id+"F2.wireOp",EDGE,"E0"),sQuery(id+"F2.wireOp",EDGE,"E3"),sQuery(id+"F2.wireOp",EDGE,"E5"),sQuery(id+"F2.wireOp",EDGE,"E8.MirrorCS")])]}),"instanceName":"88"});
            var Q89;
            Q89=makeQuery(id+"F8.opPattern","COPY",BODY,{"derivedFrom":makeQuery(id+"F4.opExtrude","SWEPT_BODY",BODY,{"disambiguationData":[OSD([sQuery(id+"F2.wireOp",EDGE,"E0"),sQuery(id+"F2.wireOp",EDGE,"E3"),sQuery(id+"F2.wireOp",EDGE,"E5"),sQuery(id+"F2.wireOp",EDGE,"E8.MirrorCS")])]}),"instanceName":"89"});
            var Q90;
            Q90=makeQuery(id+"F7.opExtrude","SWEPT_BODY",BODY,{"disambiguationData":[OSD([sQuery(id+"F3.wireOp",EDGE,"E10")])]});
            booleanBodies(context, id + "F9", {"operationType" : BooleanOperationType.SUBTRACTION, "tools" : qUnion([Q0, Q1, Q2, Q3, Q4, Q5, Q6, Q7, Q8, Q9, Q10, Q11, Q12, Q13, Q14, Q15, Q16, Q17, Q18, Q19, Q20, Q21, Q22, Q23, Q24, Q25, Q26, Q27, Q28, Q29, Q30, Q31, Q32, Q33, Q34, Q35, Q36, Q37, Q38, Q39, Q40, Q41, Q42, Q43, Q44, Q45, Q46, Q47, Q48, Q49, Q50, Q51, Q52, Q53, Q54, Q55, Q56, Q57, Q58, Q59, Q60, Q61, Q62, Q63, Q64, Q65, Q66, Q67, Q68, Q69, Q70, Q71, Q72, Q73, Q74, Q75, Q76, Q77, Q78, Q79, Q80, Q81, Q82, Q83, Q84, Q85, Q86, Q87, Q88, Q89]), "targets" : qUnion([Q90])});
        }
        {
            var Q0;
            Q0=makeQuery(id+"F7.opExtrude","CAP_FACE",FACE,{"disambiguationData":[OSD([sQuery(id+"F3.wireOp",EDGE,"E10")])],"isStart":true});
            var sketch = newSketch(context, id + "F10", { "sketchPlane" : qUnion([Q0])});
            skCircle(sketch, "E12", {"center": v(0, 0) * mm, "radius": 4.76 * mm});
            skCircle(sketch, "E13", {"center": v(0, 0) * mm, "radius": 9.76 * mm});
            skCircle(sketch, "E14", {"center": v(0, 0) * mm, "radius": 28.55 * mm});
            skLineSegment(sketch, "E15", {"start": v(0, 0) * mm, "end": v(0, 28.55) * mm, "construction": true});
            skLineSegment(sketch, "E16.0", {"start": v(2.5, 0) * mm, "end": v(2.5, 28.44) * mm});
            skLineSegment(sketch, "E17", {"start": v(0, 0) * mm, "end": v(33.55, 0) * mm, "construction": true});
            skLineSegment(sketch, "E18.0", {"start": v(0, 2.5) * mm, "end": v(33.46, 2.5) * mm});
            skCircle(sketch, "E19", {"center": v(0, 0) * mm, "radius": 33.55 * mm});
            skSolve(sketch);
        }
        {
            var Q0;
            Q0=makeQuery(id+"F10.imprint","IMPRINT",FACE,{"disambiguationData":[TD([[makeQuery(id+"F10.imprint","IMPRINT",EDGE,{"derivedFrom":sQuery(id+"F10.wireOp",EDGE,"E12")}),1.0]])]});
            extrude(context, id + "F11", {"entities" : qUnion([Q0]), "operationType" : NewBodyOperationType.REMOVE, "oppositeDirection" : true, "depth" : 25 * mm});
        }
        {
            var Q0;
            {var subQ0=sQuery(id+"F10.wireOp",EDGE,"E16.0");var subQ1=sQuery(id+"F10.wireOp",EDGE,"E13");var subQ2=makeQuery(id+"F10.imprint","INTERSECT",VERTEX,{"derivedFrom":[subQ1,subQ0]});Q0=makeQuery(id+"F10.imprint","IMPRINT",FACE,{"disambiguationData":[TD([[makeQuery(id+"F10.imprint","IMPRINT",EDGE,{"disambiguationData":[TD([[subQ2,1.0]])],"derivedFrom":subQ1}),-1.0]])]});}
            extrude(context, id + "F12", {"entities" : qUnion([Q0]), "oppositeDirection" : true, "depth" : 6 * mm});
        }
        {
            var Q0;
            Q0=makeQuery(id+"F12.opExtrude","SWEPT_EDGE",EDGE,{"disambiguationData":[OSD([sQuery(id+"F10.wireOp",EDGE,"E14"),sQuery(id+"F10.wireOp",EDGE,"E16.0")])]});
            var Q1;
            Q1=makeQuery(id+"F12.opExtrude","SWEPT_EDGE",EDGE,{"disambiguationData":[OSD([sQuery(id+"F10.wireOp",EDGE,"E13"),sQuery(id+"F10.wireOp",EDGE,"E16.0")])]});
            var Q2;
            Q2=makeQuery(id+"F12.opExtrude","SWEPT_EDGE",EDGE,{"disambiguationData":[OSD([sQuery(id+"F10.wireOp",EDGE,"E13"),sQuery(id+"F10.wireOp",EDGE,"E18.0")])]});
            var Q3;
            Q3=makeQuery(id+"F12.opExtrude","SWEPT_EDGE",EDGE,{"disambiguationData":[OSD([sQuery(id+"F10.wireOp",EDGE,"E14"),sQuery(id+"F10.wireOp",EDGE,"E18.0")])]});
            fillet(context, id + "F13", {"entities" : qUnion([Q0, Q1, Q2, Q3]), "radius" : 5 * mm, "tangentPropagation" : true, "allowEdgeOverflow" : false});
        }
        {
            var Q0;
            Q0=makeQuery(id+"F12.opExtrude","SWEPT_BODY",BODY,{"disambiguationData":[OSD([sQuery(id+"F10.wireOp",EDGE,"E13"),sQuery(id+"F10.wireOp",EDGE,"E14"),sQuery(id+"F10.wireOp",EDGE,"E16.0"),sQuery(id+"F10.wireOp",EDGE,"E18.0")])]});
            var Q1;
            Q1=makeQuery(id+"F11.boolean.opBoolean","INTERSECT",EDGE,{"derivedFrom":[makeQuery(id+"F7.opExtrude","CAP_FACE",FACE,{"disambiguationData":[OSD([sQuery(id+"F3.wireOp",EDGE,"E10")])],"isStart":false}),makeQuery(id+"F11.opExtrude","SWEPT_FACE",FACE,{"disambiguationData":[OSD([sQuery(id+"F10.wireOp",EDGE,"E12")])]})]});
            circularPattern(context, id + "F14", {"entities" : qUnion([Q0]), "axis" : qUnion([Q1]), "angle" : 360 * degree, "instanceCount" : getVariable(context, 'SP'), "equalSpace" : true});
        }
        {
            var Q0;
            Q0=makeQuery(id+"F14.opPattern","COPY",BODY,{"derivedFrom":makeQuery(id+"F12.opExtrude","SWEPT_BODY",BODY,{"disambiguationData":[OSD([sQuery(id+"F10.wireOp",EDGE,"E13"),sQuery(id+"F10.wireOp",EDGE,"E14"),sQuery(id+"F10.wireOp",EDGE,"E16.0"),sQuery(id+"F10.wireOp",EDGE,"E18.0")])]}),"instanceName":"2"});
            var Q1;
            Q1=makeQuery(id+"F14.opPattern","COPY",BODY,{"derivedFrom":makeQuery(id+"F12.opExtrude","SWEPT_BODY",BODY,{"disambiguationData":[OSD([sQuery(id+"F10.wireOp",EDGE,"E13"),sQuery(id+"F10.wireOp",EDGE,"E14"),sQuery(id+"F10.wireOp",EDGE,"E16.0"),sQuery(id+"F10.wireOp",EDGE,"E18.0")])]}),"instanceName":"1"});
            var Q2;
            Q2=makeQuery(id+"F12.opExtrude","SWEPT_BODY",BODY,{"disambiguationData":[OSD([sQuery(id+"F10.wireOp",EDGE,"E13"),sQuery(id+"F10.wireOp",EDGE,"E14"),sQuery(id+"F10.wireOp",EDGE,"E16.0"),sQuery(id+"F10.wireOp",EDGE,"E18.0")])]});
            var Q3;
            Q3=makeQuery(id+"F14.opPattern","COPY",BODY,{"derivedFrom":makeQuery(id+"F12.opExtrude","SWEPT_BODY",BODY,{"disambiguationData":[OSD([sQuery(id+"F10.wireOp",EDGE,"E13"),sQuery(id+"F10.wireOp",EDGE,"E14"),sQuery(id+"F10.wireOp",EDGE,"E16.0"),sQuery(id+"F10.wireOp",EDGE,"E18.0")])]}),"instanceName":"3"});
            var Q4;
            Q4=makeQuery(id+"F14.opPattern","COPY",BODY,{"derivedFrom":makeQuery(id+"F12.opExtrude","SWEPT_BODY",BODY,{"disambiguationData":[OSD([sQuery(id+"F10.wireOp",EDGE,"E13"),sQuery(id+"F10.wireOp",EDGE,"E14"),sQuery(id+"F10.wireOp",EDGE,"E16.0"),sQuery(id+"F10.wireOp",EDGE,"E18.0")])]}),"instanceName":"4"});
            var Q5;
            Q5=makeQuery(id+"F14.opPattern","COPY",BODY,{"derivedFrom":makeQuery(id+"F12.opExtrude","SWEPT_BODY",BODY,{"disambiguationData":[OSD([sQuery(id+"F10.wireOp",EDGE,"E13"),sQuery(id+"F10.wireOp",EDGE,"E14"),sQuery(id+"F10.wireOp",EDGE,"E16.0"),sQuery(id+"F10.wireOp",EDGE,"E18.0")])]}),"instanceName":"5"});
            var Q6;
            Q6=makeQuery(id+"F7.opExtrude","SWEPT_BODY",BODY,{"disambiguationData":[OSD([sQuery(id+"F3.wireOp",EDGE,"E10")])]});
            booleanBodies(context, id + "F15", {"operationType" : BooleanOperationType.SUBTRACTION, "tools" : qUnion([Q0, Q1, Q2, Q3, Q4, Q5]), "targets" : qUnion([Q6])});
        }
    });
